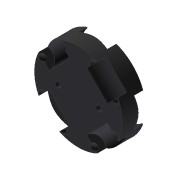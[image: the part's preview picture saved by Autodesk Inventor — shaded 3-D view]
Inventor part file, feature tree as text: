
AUTODESK INVENTOR PART (.ipt)
format: ipt  version: 2017 (Build 210142000, 142)  size: 205,824 bytes
history: native  units: mm
features: sketch x4, revolve x2, pattern_circular x2, extrude x1, hole x1
ambient origin geometry x8: Origin, YZ Plane, XZ Plane, XY Plane, X Axis, Y Axis, Z Axis, Center Point
bodies: Solid1 (feature_tree)
feature tree (10):
  extrude  "Extrusion1"  Depth=16.0mm TaperAngle=0.0deg
  revolve  "Revolution1"  [1 undecoded]
  pattern_circular  "Circular Pattern2"  [2 undecoded]
  revolve  "Revolution2"  [1 undecoded]
  pattern_circular  "Circular Pattern3"  Angle=90.0deg  [1 undecoded]
  hole  "Hole1"  [1 undecoded]
  sketch  "Sketch1"  dims[d0=60.0mm d1=16.0mm d2=0.0mm]
  sketch  "Sketch2"  dims[d3=14.0mm d4=25.0mm]
  sketch  "Sketch3"  dims[d5=6.0mm]
  sketch  "Sketch4"  dims[d6=5.0mm d7=5.0mm d8=20.0mm d9=90.0deg d13=40.0mm d14=360.0deg d16=45.0deg d17=25.0mm d18=14.0mm d19=20.0mm d20=5.0mm d21=5.0mm d22=90.0deg d23=40.0mm d24=360.0deg d26=14.0mm d27=14.0mm d28=4.0mm d29=6.0mm d30=4.0mm d31=2.0mm d32=90.0deg d33=8.0mm d34=20.594885mm]
note: 6 required parameter values undecoded (feature->parameter linkage not recoverable at this tier; creation-order binding heuristic only, values carry confidence <= 0.55)